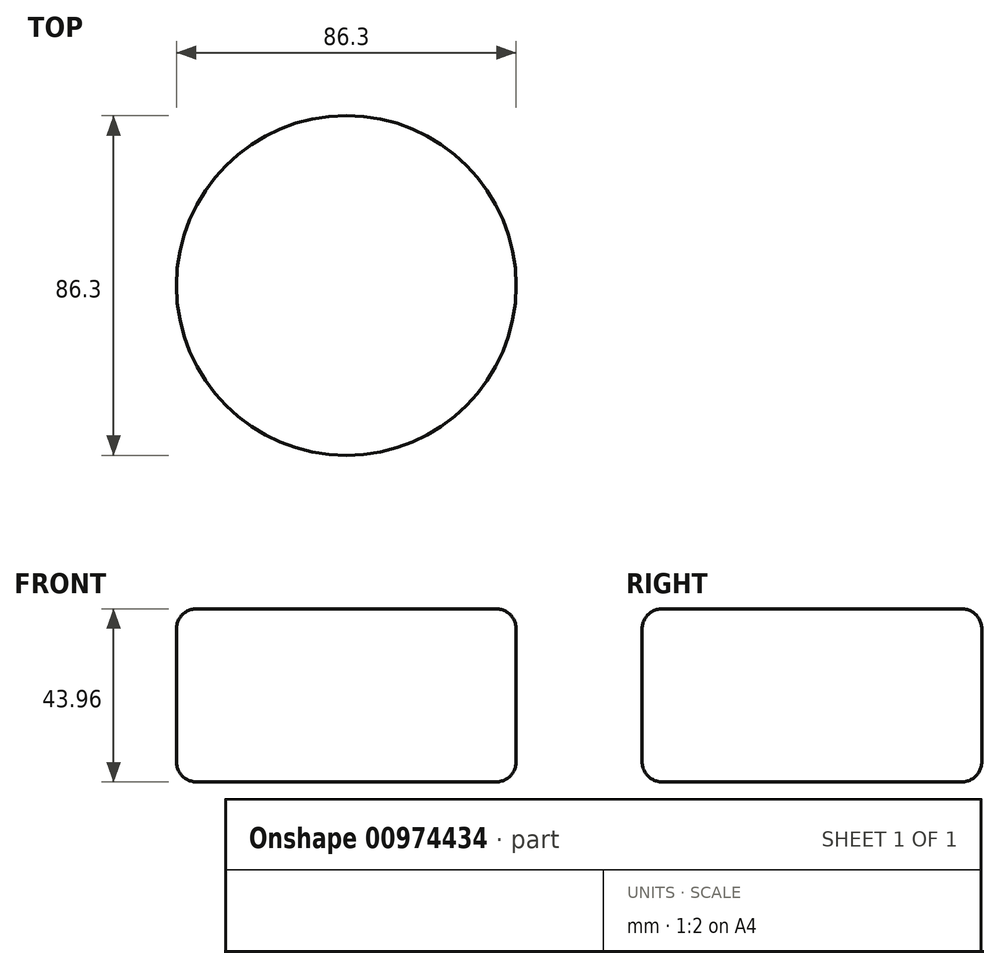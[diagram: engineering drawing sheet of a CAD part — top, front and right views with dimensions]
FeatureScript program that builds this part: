
annotation { "Feature Type Name" : "Feature", "Feature Type Description" : "" }
export const myFeature = defineFeature(function(context is Context, id is Id, definition is map)
    precondition{}
    {
        {
            var Q0;
            Q0=qCreatedBy(makeId("Top.planeOp"),FACE);
            var sketch = newSketch(context, id + "F0", { "sketchPlane" : qUnion([Q0])});
            skCircle(sketch, "E0", {"center": v(0, 0) * mm, "radius": 43.15 * mm});
            skSolve(sketch);
        }
        {
            var Q0;
            Q0 = qSketchRegion(id + "F0", true);
            extrude(context, id + "F1", {"entities" : qUnion([Q0]), "depth" : 43.96 * mm, "offsetDistance" : 25.4 * mm});
        }
        {
            var Q0;
            Q0=makeQuery(id+"F1.opExtrude","CAP_FACE",FACE,{"disambiguationData":[OSD([sQuery(id+"F0.wireOp",EDGE,"E0")])],"isStart":true});
            fillet(context, id + "F2", {"entities" : qUnion([Q0]), "radius" : 5.08 * mm, "tangentPropagation" : true, "allowEdgeOverflow" : false});
        }
        {
            var Q0;
            Q0=makeQuery(id+"F1.opExtrude","CAP_EDGE",EDGE,{"disambiguationData":[OSD([sQuery(id+"F0.wireOp",EDGE,"E0")])],"isStart":false});
            fillet(context, id + "F3", {"entities" : qUnion([Q0]), "radius" : 5.08 * mm, "tangentPropagation" : true, "allowEdgeOverflow" : false});
        }
    });
